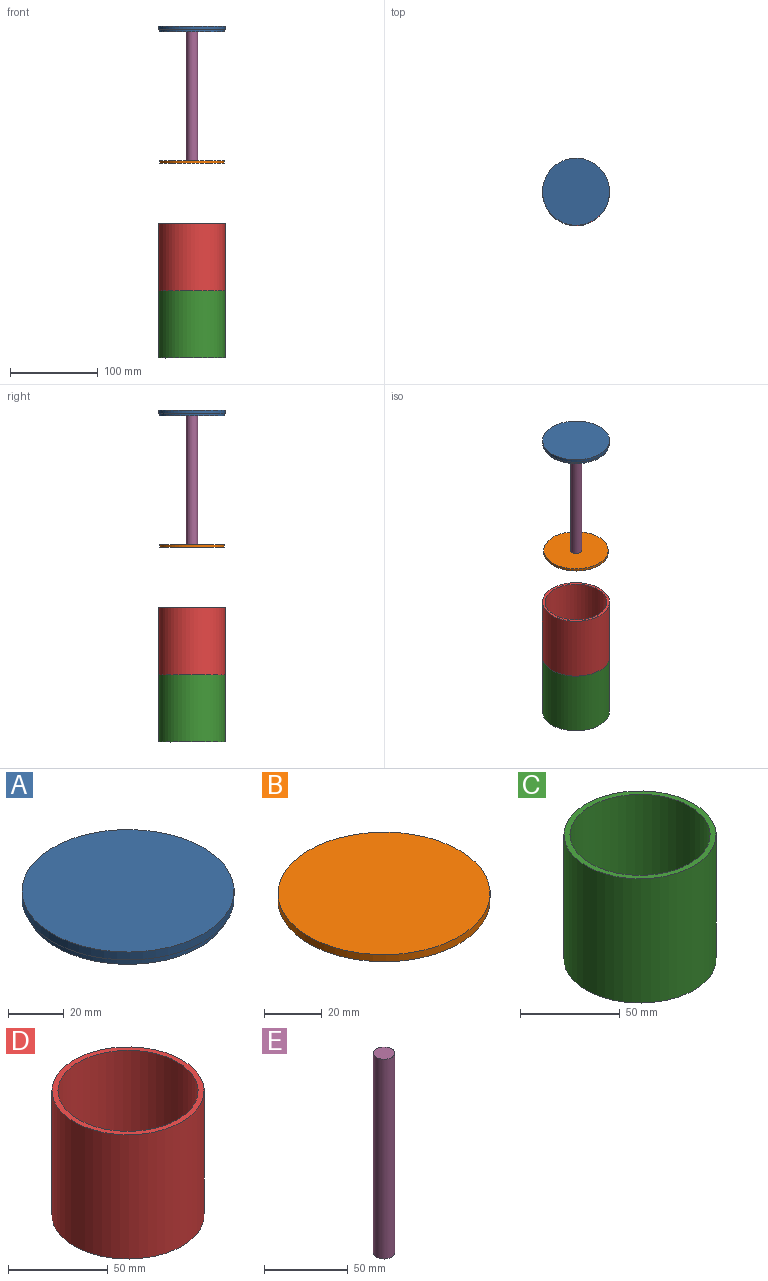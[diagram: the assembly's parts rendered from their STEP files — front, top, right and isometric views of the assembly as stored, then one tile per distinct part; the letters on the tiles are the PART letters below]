
ASSEMBLY  parts=5 mates=3
PART A: 5 faces, bbox 76.2x76.2x6.5 mm
  f0: cylinder r=36.6mm len=73.2mm, axis (0,0,1), area 689.3mm2, adj f1,f4
  f1: plane 73.2x73.2mm, normal (0,0,-1), area 4208.7mm2, adj f0
  f2: cylinder r=38.1mm len=76.2mm, axis (0,0,-1), area 826.9mm2, adj f3,f4
  f3: plane 76.2x76.2mm, normal (0,0,1), area 4560.4mm2, adj f2
  f4: plane 76.2x76.2mm, normal (0,0,-1), area 351.7mm2, adj f0,f2
PART B: 3 faces, bbox 73.2x73.2x3 mm
  f0: cylinder r=36.6mm len=73.2mm, axis (0,0,-1), area 689.3mm2, adj f1,f2
  f1: plane 73.2x73.2mm, normal (0,0,1), area 4208.7mm2, adj f0
  f2: plane 73.2x73.2mm, normal (0,0,-1), area 4208.7mm2, adj f0
PART C: 5 faces, bbox 76.2x76.2x76.2 mm
  f0: cylinder r=38.1mm len=76.2mm, axis (0,0,-1), area 18241.5mm2, adj f1,f2
  f1: plane 76.2x76.2mm, normal (0,0,1), area 689.3mm2, adj f0,f3
  f2: plane 76.2x76.2mm, normal (0,0,-1), area 4560.4mm2, adj f0
  f3: cylinder r=35.1mm len=73.2mm, axis (0,0,-1), area 16145.4mm2, adj f1,f4
  f4: plane 70.21x70.21mm, normal (0,0,1), area 3871.1mm2, adj f3
PART D: 4 faces, bbox 76.2x76.2x76.2 mm
  f0: cylinder r=38.1mm len=76.2mm, axis (0,0,-1), area 18241.5mm2, adj f1,f2
  f1: plane 76.2x76.2mm, normal (0,0,1), area 689.3mm2, adj f0,f3
  f2: plane 76.2x76.2mm, normal (0,0,-1), area 689.3mm2, adj f0,f3
  f3: cylinder r=35.1mm len=76.2mm, axis (0,0,-1), area 16806.5mm2, adj f1,f2
PART E: 3 faces, bbox 12.7x12.7x146.4 mm
  f0: cylinder r=6.35mm len=146.41mm, axis (0,0,-1), area 5841.3mm2, adj f1,f2
  f1: plane 12.7x12.7mm, normal (0,0,1), area 126.7mm2, adj f0
  f2: plane 12.7x12.7mm, normal (0,0,-1), area 126.7mm2, adj f0
PLACE A t=(-168.47,-34.69,265.16)mm
PLACE B t=(-49.41,26.78,112.76)mm
PLACE C t=(108.07,10.78,-108.67)mm
PLACE D t=(-49.41,26.78,-32.47)mm
PLACE E t=(15.81,-8.2,115.75)mm
MATE fastened B.f0 <-> E.f0  axis (0,0,1) through (-49.41,26.78,115.75)mm
MATE fastened C.f0 <-> D.f0  axis (0,0,1) through (-49.41,26.78,-32.47)mm
MATE fastened E.f0 <-> A.f0  axis (0,0,1) through (-49.41,26.78,262.16)mm
